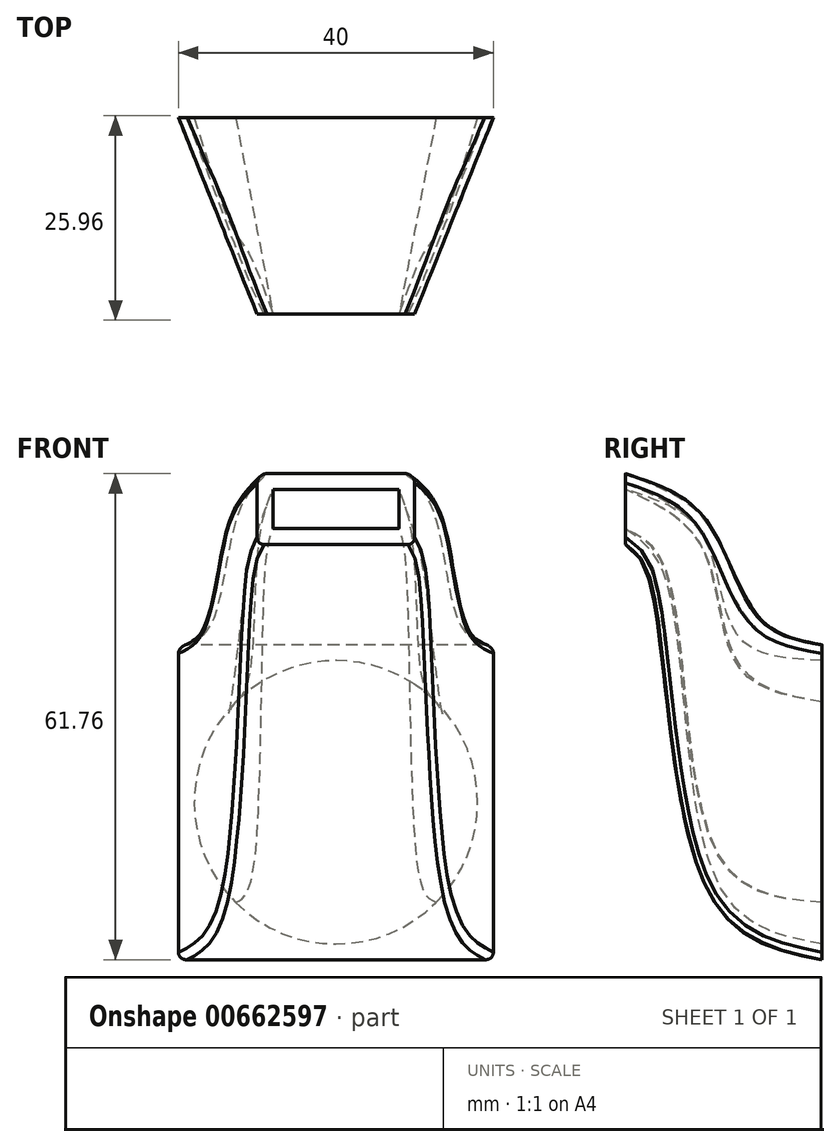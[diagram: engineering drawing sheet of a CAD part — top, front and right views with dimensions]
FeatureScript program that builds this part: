
annotation { "Feature Type Name" : "Feature", "Feature Type Description" : "" }
export const myFeature = defineFeature(function(context is Context, id is Id, definition is map)
    precondition{}
    {
        {
            var Q0;
            Q0=qCreatedBy(makeId("Front.planeOp"),FACE);
            var sketch = newSketch(context, id + "F0", { "sketchPlane" : qUnion([Q0])});
            skLineSegment(sketch, "E0.bottom", {"start": v(20, -20) * mm, "end": v(-20, -20) * mm});
            skLineSegment(sketch, "E0.top", {"start": v(20, 20) * mm, "end": v(-20, 20) * mm});
            skLineSegment(sketch, "E0.left", {"start": v(20, -20) * mm, "end": v(20, 20) * mm});
            skLineSegment(sketch, "E0.right", {"start": v(-20, -20) * mm, "end": v(-20, 20) * mm});
            skPoint(sketch, "E0.middle", {"position": v(0, 0) * mm});
            skLineSegment(sketch, "E1", {"start": v(-12.73, 12.73) * mm, "end": v(-12.73, 12.73) * mm});
            skLineSegment(sketch, "E2", {"start": v(12.73, 12.73) * mm, "end": v(12.73, 12.73) * mm});
            skArc(sketch, "E3", {"start": v(12.73, -12.73) * mm, "mid": v(18, 0) * mm, "end": v(12.73, 12.73) * mm});
            skArc(sketch, "E4", {"start": v(-12.73, -12.73) * mm, "mid": v(0, -18) * mm, "end": v(12.73, -12.73) * mm});
            skArc(sketch, "E5", {"start": v(-12.73, 12.73) * mm, "mid": v(-18, 0) * mm, "end": v(-12.73, -12.73) * mm});
            skArc(sketch, "E6", {"start": v(12.73, 12.73) * mm, "mid": v(0, 18) * mm, "end": v(-12.73, 12.73) * mm});
            skPoint(sketch, "E7", {"position": v(-12.73, 12.73) * mm});
            skPoint(sketch, "E8", {"position": v(12.73, 12.73) * mm});
            skPoint(sketch, "E9", {"position": v(12.73, -12.73) * mm});
            skPoint(sketch, "E10", {"position": v(-12.73, -12.73) * mm});
            skSolve(sketch);
        }
        {
            var Q0;
            Q0=qCreatedBy(makeId("Front.planeOp"),FACE);
            cPlane(context, id + "F1", {"entities" : qUnion([Q0]), "cplaneType" : CPlaneType.OFFSET, "offset" : 25 * mm, "width" : 150 * mm, "height" : 150 * mm});
        }
        {
            var Q0;
            Q0=qCreatedBy(id+"F1.planeOp",FACE);
            var sketch = newSketch(context, id + "F2", { "sketchPlane" : qUnion([Q0])});
            skLineSegment(sketch, "E11.bottom", {"start": v(10, 32.76) * mm, "end": v(-10, 32.76) * mm});
            skLineSegment(sketch, "E11.top", {"start": v(10, 41.76) * mm, "end": v(-10, 41.76) * mm});
            skLineSegment(sketch, "E11.left", {"start": v(10, 32.76) * mm, "end": v(10, 41.76) * mm});
            skLineSegment(sketch, "E11.right", {"start": v(-10, 32.76) * mm, "end": v(-10, 41.76) * mm});
            skPoint(sketch, "E11.middle", {"position": v(0, 37.26) * mm});
            skLineSegment(sketch, "E12.bottom", {"start": v(8, 34.76) * mm, "end": v(-8, 34.76) * mm});
            skLineSegment(sketch, "E12.top", {"start": v(8, 39.76) * mm, "end": v(-8, 39.76) * mm});
            skLineSegment(sketch, "E12.left", {"start": v(8, 34.76) * mm, "end": v(8, 39.76) * mm});
            skLineSegment(sketch, "E12.right", {"start": v(-8, 34.76) * mm, "end": v(-8, 39.76) * mm});
            skSolve(sketch);
        }
        {
            var Q0;
            Q0=sQuery(id+"F0.wireOp",VERTEX,"E9");
            var Q1;
            Q1=sQuery(id+"F0.wireOp",VERTEX,"E8");
            var Q2;
            Q2=sQuery(id+"F2.wireOp",VERTEX,"E12.left.end");
            cPlane(context, id + "F3", {"entities" : qUnion([Q0, Q1, Q2]), "cplaneType" : CPlaneType.THREE_POINT, "offset" : 25 * mm, "width" : 150 * mm, "height" : 150 * mm});
        }
        {
            var Q0;
            Q0=sQuery(id+"F0.wireOp",VERTEX,"E7");
            var Q1;
            Q1=sQuery(id+"F0.wireOp",VERTEX,"E10");
            var Q2;
            Q2=sQuery(id+"F2.wireOp",VERTEX,"E12.right.end");
            cPlane(context, id + "F4", {"entities" : qUnion([Q0, Q1, Q2]), "cplaneType" : CPlaneType.THREE_POINT, "offset" : 25 * mm, "width" : 150 * mm, "height" : 150 * mm});
        }
        {
            var Q0;
            Q0=qCreatedBy(id+"F4.planeOp",FACE);
            var sketch = newSketch(context, id + "F5", { "sketchPlane" : qUnion([Q0])});
            skEllipticalArc(sketch, "E13.0", {});
            skLineSegment(sketch, "E14.0", {"start": v(-23.08, 34.76) * mm, "end": v(-23.08, 39.76) * mm});
            skFitSpline(sketch, "E15", {"points": [v(2.37, 12.73) * mm, v(-8.25, 17.4) * mm, v(-13.04, 32.29) * mm, v(-23.08, 39.76) * mm], "startDerivative": vector(-40.29, 7.29) * mm, "endDerivative": vector(-36.85, 16.66) * mm});
            skFitSpline(sketch, "E16", {"points": [v(2.37, -12.73) * mm, v(-11, -6.66) * mm, v(-17.7, 29.34) * mm, v(-23.08, 34.76) * mm], "startDerivative": vector(-51.43, 4.3) * mm, "endDerivative": vector(-28.05, 13.02) * mm});
            const initialGuessF5  = {"E13.0": [0, 0, 0, 1, 0.018, 0.0033448153564885168, 3.926990816987241, 5.497787143782138]};
            skSetInitialGuess(sketch, initialGuessF5);
            skSolve(sketch);
        }
        {
            var Q0;
            Q0=qCreatedBy(id+"F3.planeOp",FACE);
            var sketch = newSketch(context, id + "F6", { "sketchPlane" : qUnion([Q0])});
            skLineSegment(sketch, "E17.0", {"start": v(23.08, 34.76) * mm, "end": v(23.08, 39.76) * mm});
            skEllipticalArc(sketch, "E18.0", {});
            skFitSpline(sketch, "E19", {"points": [v(-2.37, 12.73) * mm, v(8.49, 17.3) * mm, v(13.03, 32.2) * mm, v(23.08, 39.76) * mm], "startDerivative": vector(41.25, 6.7) * mm, "endDerivative": vector(37.1, 16.93) * mm});
            skFitSpline(sketch, "E20", {"points": [v(-2.37, -12.73) * mm, v(11.05, -6.8) * mm, v(17.81, 29.26) * mm, v(23.08, 34.76) * mm], "startDerivative": vector(51.55, 3.8) * mm, "endDerivative": vector(27.5, 13.45) * mm});
            const initialGuessF6  = {"E18.0": [0, 0, 0, -1, 0.018, 0.0033448153564885107, 3.926990816987242, 5.497787143782138]};
            skSetInitialGuess(sketch, initialGuessF6);
            skSolve(sketch);
        }
        {
            var Q0;
            Q0=sQuery(id+"F2.wireOp",VERTEX,"E11.right.end");
            var Q1;
            Q1=sQuery(id+"F2.wireOp",VERTEX,"E11.right.start");
            var Q2;
            Q2=sQuery(id+"F0.wireOp",VERTEX,"E0.right.start");
            cPlane(context, id + "F7", {"entities" : qUnion([Q0, Q1, Q2]), "cplaneType" : CPlaneType.THREE_POINT, "offset" : 25 * mm, "width" : 150 * mm, "height" : 150 * mm});
        }
        {
            var Q0;
            Q0=sQuery(id+"F2.wireOp",VERTEX,"E11.left.end");
            var Q1;
            Q1=sQuery(id+"F2.wireOp",VERTEX,"E11.bottom.start");
            var Q2;
            Q2=sQuery(id+"F0.wireOp",VERTEX,"E0.bottom.start");
            cPlane(context, id + "F8", {"entities" : qUnion([Q0, Q1, Q2]), "cplaneType" : CPlaneType.THREE_POINT, "offset" : 25 * mm, "width" : 150 * mm, "height" : 150 * mm});
        }
        {
            var Q0;
            Q0=qCreatedBy(id+"F7.planeOp",FACE);
            var sketch = newSketch(context, id + "F9", { "sketchPlane" : qUnion([Q0])});
            skLineSegment(sketch, "E21.0", {"start": v(-7.43, -20) * mm, "end": v(-7.43, 20) * mm});
            skLineSegment(sketch, "E22.0", {"start": v(19.5, 32.76) * mm, "end": v(19.5, 41.76) * mm});
            skFitSpline(sketch, "E23", {"points": [v(-7.43, 20) * mm, v(1.02, 23.33) * mm, v(8.39, 35.58) * mm, v(19.5, 41.76) * mm], "startDerivative": vector(32.53, 6.16) * mm, "endDerivative": vector(40.52, 15.4) * mm});
            skFitSpline(sketch, "E24", {"points": [v(-7.43, -20) * mm, v(8.15, -11.3) * mm, v(16.28, 28.4) * mm, v(19.5, 32.76) * mm], "startDerivative": vector(54.74, 9.9) * mm, "endDerivative": vector(19.5, 13.25) * mm});
            skSolve(sketch);
        }
        {
            var Q0;
            Q0=qCreatedBy(id+"F8.planeOp",FACE);
            var sketch = newSketch(context, id + "F10", { "sketchPlane" : qUnion([Q0])});
            skLineSegment(sketch, "E25.0", {"start": v(19.5, 32.76) * mm, "end": v(19.5, 41.76) * mm});
            skLineSegment(sketch, "E26.0", {"start": v(-7.43, -20) * mm, "end": v(-7.43, 20) * mm});
            skFitSpline(sketch, "E27", {"points": [v(-7.43, 20) * mm, v(1.36, 23.49) * mm, v(8.53, 35.99) * mm, v(19.5, 41.76) * mm], "startDerivative": vector(32.93, 5.3) * mm, "endDerivative": vector(36.4, 10.97) * mm});
            skFitSpline(sketch, "E28", {"points": [v(-7.43, -20) * mm, v(8.27, -11.01) * mm, v(16.18, 28.63) * mm, v(19.5, 32.76) * mm], "startDerivative": vector(54.97, 10.57) * mm, "endDerivative": vector(20.38, 12.24) * mm});
            skSolve(sketch);
        }
        {
            var Q0;
            Q0=makeQuery(id+"F0.imprint","IMPRINT",FACE,{"disambiguationData":[TD([[makeQuery(id+"F0.imprint","IMPRINT",EDGE,{"derivedFrom":sQuery(id+"F0.wireOp",EDGE,"E0.bottom")}),-1.0]])]});
            var sketch = newSketch(context, id + "F11", { "sketchPlane" : qUnion([Q0])});
            skLineSegment(sketch, "E29.0", {"start": v(20, 20) * mm, "end": v(-20, 20) * mm});
            skLineSegment(sketch, "E29.1", {"start": v(20, -20) * mm, "end": v(20, 20) * mm});
            skLineSegment(sketch, "E29.2", {"start": v(20, -20) * mm, "end": v(-20, -20) * mm});
            skLineSegment(sketch, "E29.3", {"start": v(-20, -20) * mm, "end": v(-20, 20) * mm});
            skSolve(sketch);
        }
        {
            var Q0;
            Q0=makeQuery(id+"F2.imprint","IMPRINT",FACE,{"disambiguationData":[TD([[makeQuery(id+"F2.imprint","IMPRINT",EDGE,{"derivedFrom":sQuery(id+"F2.wireOp",EDGE,"E11.bottom")}),-1.0]])]});
            var sketch = newSketch(context, id + "F12", { "sketchPlane" : qUnion([Q0])});
            skLineSegment(sketch, "E30.0", {"start": v(10, 41.76) * mm, "end": v(-10, 41.76) * mm});
            skLineSegment(sketch, "E30.1", {"start": v(-10, 32.76) * mm, "end": v(-10, 41.76) * mm});
            skLineSegment(sketch, "E30.2", {"start": v(10, 32.76) * mm, "end": v(-10, 32.76) * mm});
            skLineSegment(sketch, "E30.3", {"start": v(10, 32.76) * mm, "end": v(10, 41.76) * mm});
            skSolve(sketch);
        }
        {
            var Q0;
            Q0 = qSketchRegion(id + "F11", true);
            var Q1;
            Q1 = qSketchRegion(id + "F12", true);
            var Q2;
            Q2=sQuery(id+"F10.wireOp",EDGE,"E27");
            var Q3;
            Q3=sQuery(id+"F9.wireOp",EDGE,"E23");
            var Q4;
            Q4=sQuery(id+"F9.wireOp",EDGE,"E24");
            var Q5;
            Q5=sQuery(id+"F10.wireOp",EDGE,"E28");
            loft(context, id + "F13", {"addGuides" : true, "sheetProfilesArray" : [{ "sheetProfileEntities" : qUnion([Q0]) }, { "sheetProfileEntities" : qUnion([Q1]) }], "guidesArray" : [{ "guideEntities" : qUnion([Q2]), "guideDerivativeType" : LoftGuideDerivativeType.DEFAULT, "guideDerivativeMagnitude" : 1 }, { "guideEntities" : qUnion([Q3]), "guideDerivativeType" : LoftGuideDerivativeType.DEFAULT, "guideDerivativeMagnitude" : 1 }, { "guideEntities" : qUnion([Q4]), "guideDerivativeType" : LoftGuideDerivativeType.DEFAULT, "guideDerivativeMagnitude" : 1 }, { "guideEntities" : qUnion([Q5]), "guideDerivativeType" : LoftGuideDerivativeType.DEFAULT, "guideDerivativeMagnitude" : 1 }]});
        }
        {
            var Q1;
            Q1=makeQuery(id+"F0.imprint","IMPRINT",FACE,{"disambiguationData":[TD([[makeQuery(id+"F0.imprint","IMPRINT",EDGE,{"derivedFrom":sQuery(id+"F0.wireOp",EDGE,"E3")}),1.0]])]});
            var Q2;
            Q2=makeQuery(id+"F2.imprint","IMPRINT",FACE,{"disambiguationData":[TD([[makeQuery(id+"F2.imprint","IMPRINT",EDGE,{"derivedFrom":sQuery(id+"F2.wireOp",EDGE,"E12.bottom")}),-1.0]])]});
            var Q3;
            Q3=sQuery(id+"F5.wireOp",EDGE,"E15");
            var Q4;
            Q4=sQuery(id+"F5.wireOp",EDGE,"E16");
            var Q5;
            Q5=sQuery(id+"F6.wireOp",EDGE,"E19");
            var Q6;
            Q6=sQuery(id+"F6.wireOp",EDGE,"E20");
            loft(context, id + "F14", {"operationType" : NewBodyOperationType.REMOVE, "addGuides" : true, "sheetProfilesArray" : [{ "sheetProfileEntities" : qUnion([Q1]) }, { "sheetProfileEntities" : qUnion([Q2]) }], "guidesArray" : [{ "guideEntities" : qUnion([Q3]), "guideDerivativeType" : LoftGuideDerivativeType.DEFAULT, "guideDerivativeMagnitude" : 1 }, { "guideEntities" : qUnion([Q4]), "guideDerivativeType" : LoftGuideDerivativeType.DEFAULT, "guideDerivativeMagnitude" : 1 }, { "guideEntities" : qUnion([Q5]), "guideDerivativeType" : LoftGuideDerivativeType.DEFAULT, "guideDerivativeMagnitude" : 1 }, { "guideEntities" : qUnion([Q6]), "guideDerivativeType" : LoftGuideDerivativeType.DEFAULT, "guideDerivativeMagnitude" : 1 }]});
        }
        {
            var Q0;
            Q0=makeQuery(id+"F13.opLoft","SWEPT_EDGE",EDGE,{"disambiguationData":[OSD([sQuery(id+"F10.wireOp",EDGE,"E27")])]});
            var Q1;
            Q1=makeQuery(id+"F13.opLoft","SWEPT_EDGE",EDGE,{"disambiguationData":[OSD([sQuery(id+"F10.wireOp",EDGE,"E28")])]});
            var Q2;
            Q2=makeQuery(id+"F13.opLoft","SWEPT_EDGE",EDGE,{"disambiguationData":[OSD([sQuery(id+"F9.wireOp",EDGE,"E24")])]});
            var Q3;
            Q3=makeQuery(id+"F13.opLoft","SWEPT_EDGE",EDGE,{"disambiguationData":[OSD([sQuery(id+"F9.wireOp",EDGE,"E23")])]});
            fillet(context, id + "F15", {"entities" : qUnion([Q0, Q1, Q2, Q3]), "radius" : 1 * mm, "tangentPropagation" : true, "allowEdgeOverflow" : false});
        }
    });
